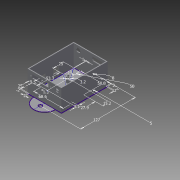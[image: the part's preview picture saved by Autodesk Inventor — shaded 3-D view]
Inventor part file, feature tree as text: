
AUTODESK INVENTOR PART (.ipt)
format: ipt  version: 2013 SP2 (Build 170200200, 200)  size: 238,592 bytes
history: native  units: mm
features: extrude x8, sketch x5, projected_geometry x1
ambient origin geometry x8: Origin, YZ Plane, XZ Plane, XY Plane, X Axis, Y Axis, Z Axis, Center Point
bodies: Solid1 (feature_tree)
feature tree (14):
  sketch  "Sketch1"  dims[d0=53.3mm d2=68.6mm]
  extrude  "Extrusion1"  Depth=68.6mm
  extrude  "Extrusion2"  Depth=2.5mm
  extrude  "Extrusion3"  Depth=27.9mm
  extrude  "Extrusion6"  Depth=3.2mm
  extrude  "Extrusion7"  Depth=1.0mm
  extrude  "Extrusion4"  Depth=2.0mm
  extrude  "Extrusion8"  Depth=2.0mm
  extrude  "Extrusion9"  Depth=2.0mm TaperAngle=0.0deg
  sketch  "Sketch2"  dims[d3=14.0mm d4=2.5mm]
  sketch  "Sketch4"  dims[d5=50.8mm d6=27.9mm]
  sketch  "Sketch7"  dims[d7=5.1mm d8=3.2mm]
  projected_geometry  "Projected Loop1"
  sketch  "Sketch8"  dims[d9=25.0mm d10=1.0mm d11=2.0mm d12=2.0mm d13=2.0mm d14=0.0mm d15=50.0mm d16=0.0mm d17=8.3mm d19=4.3mm d20=5.0mm d21=0.0mm d22=13.0mm d24=12.0mm d26=9.0mm d27=12.0mm d28=10.0mm d31=3.25mm d32=5.0mm d33=0.0mm d46=9.9mm d54=12.3mm d59=5.0mm d62=25.0mm d63=2.0mm d64=2.0mm d65=3.89mm d74=0.0mm d75=0.0mm d79=4.0mm d80=20.0mm d81=6.0mm d82=6.0mm d83=20.0mm d84=8.0mm d85=0.0mm d86=10.0mm d87=0.0mm d88=1.5mm d90=1.5mm d92=15.2mm d94=1.3mm d95=50.0mm d96=8.0mm d97=3.0mm d98=0.0mm d99=127.0mm d100=8.3mm d102=37.0mm d103=4.0mm d104=3.0mm d105=10.0mm d106=7.5mm d107=8.1mm d108=10.0mm d109=10.0mm d110=0.0mm d122=23.6mm d123=8.6mm d124=2.25mm d125=2.25mm d126=2.25mm d127=2.25mm d128=5.0mm d129=10.0mm d130=10.0mm]
